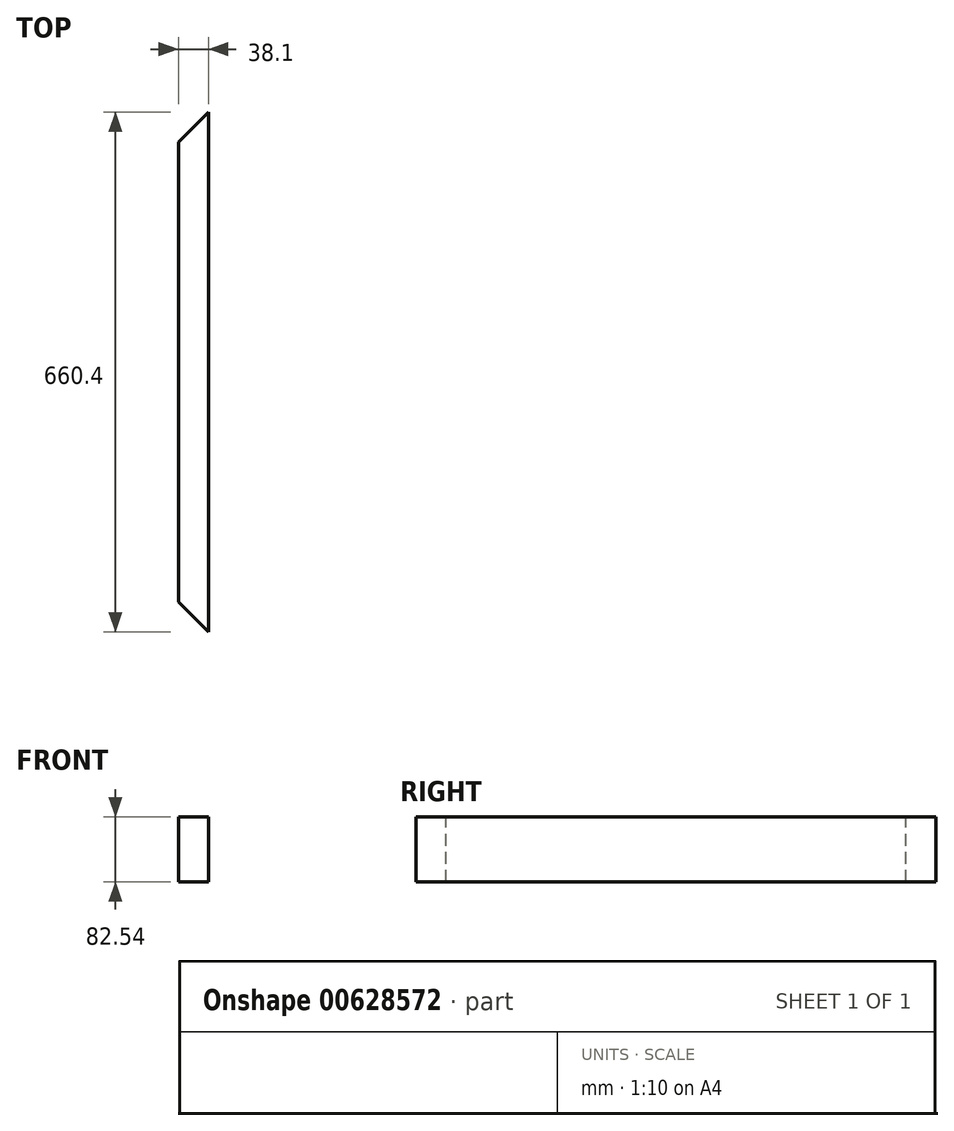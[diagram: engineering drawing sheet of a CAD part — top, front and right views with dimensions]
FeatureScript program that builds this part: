
annotation { "Feature Type Name" : "Feature", "Feature Type Description" : "" }
export const myFeature = defineFeature(function(context is Context, id is Id, definition is map)
    precondition{}
    {
        {
            var Q0;
            Q0=qCreatedBy(makeId("Right.planeOp"),FACE);
            var sketch = newSketch(context, id + "F0", { "sketchPlane" : qUnion([Q0])});
            skLineSegment(sketch, "E0.bottom", {"start": v(330.2, -41.28) * mm, "end": v(-330.2, -41.28) * mm});
            skLineSegment(sketch, "E0.top", {"start": v(330.2, 41.28) * mm, "end": v(-330.2, 41.28) * mm});
            skLineSegment(sketch, "E0.left", {"start": v(330.2, -41.28) * mm, "end": v(330.2, 41.27) * mm});
            skLineSegment(sketch, "E0.right", {"start": v(-330.2, -41.28) * mm, "end": v(-330.2, 41.27) * mm});
            skPoint(sketch, "E0.middle", {"position": v(0, 0) * mm});
            skSolve(sketch);
        }
        {
            var Q0;
            Q0 = qSketchRegion(id + "F0", true);
            extrude(context, id + "F1", {"entities" : qUnion([Q0]), "endBound" : BoundingType.SYMMETRIC, "depth" : 38.1 * mm, "offsetDistance" : 25.4 * mm});
        }
        {
            var Q0;
            Q0=makeQuery(id+"F1.opExtrude","SWEPT_FACE",FACE,{"disambiguationData":[OSD([sQuery(id+"F0.wireOp",EDGE,"E0.top")])]});
            var sketch = newSketch(context, id + "F2", { "sketchPlane" : qUnion([Q0])});
            skLineSegment(sketch, "E1", {"start": v(-19.05, 292.1) * mm, "end": v(19.05, 330.2) * mm});
            skLineSegment(sketch, "E2", {"start": v(19.05, 330.2) * mm, "end": v(-19.05, 330.2) * mm});
            skLineSegment(sketch, "E3", {"start": v(-19.05, 330.2) * mm, "end": v(-19.05, 292.1) * mm});
            skLineSegment(sketch, "E4.MirrorCS", {"start": v(19.05, -330.2) * mm, "end": v(-19.05, -330.2) * mm});
            skLineSegment(sketch, "E5.MirrorCS", {"start": v(-19.05, -330.2) * mm, "end": v(-19.05, -292.1) * mm});
            skLineSegment(sketch, "E6.MirrorCS", {"start": v(-19.05, -292.1) * mm, "end": v(19.05, -330.2) * mm});
            skSolve(sketch);
        }
        {
            var Q0;
            Q0 = qSketchRegion(id + "F2", true);
            extrude(context, id + "F3", {"entities" : qUnion([Q0]), "operationType" : NewBodyOperationType.REMOVE, "endBound" : BoundingType.UP_TO_NEXT, "oppositeDirection" : true, "depth" : 25.4 * mm, "offsetDistance" : 25.4 * mm});
        }
    });
